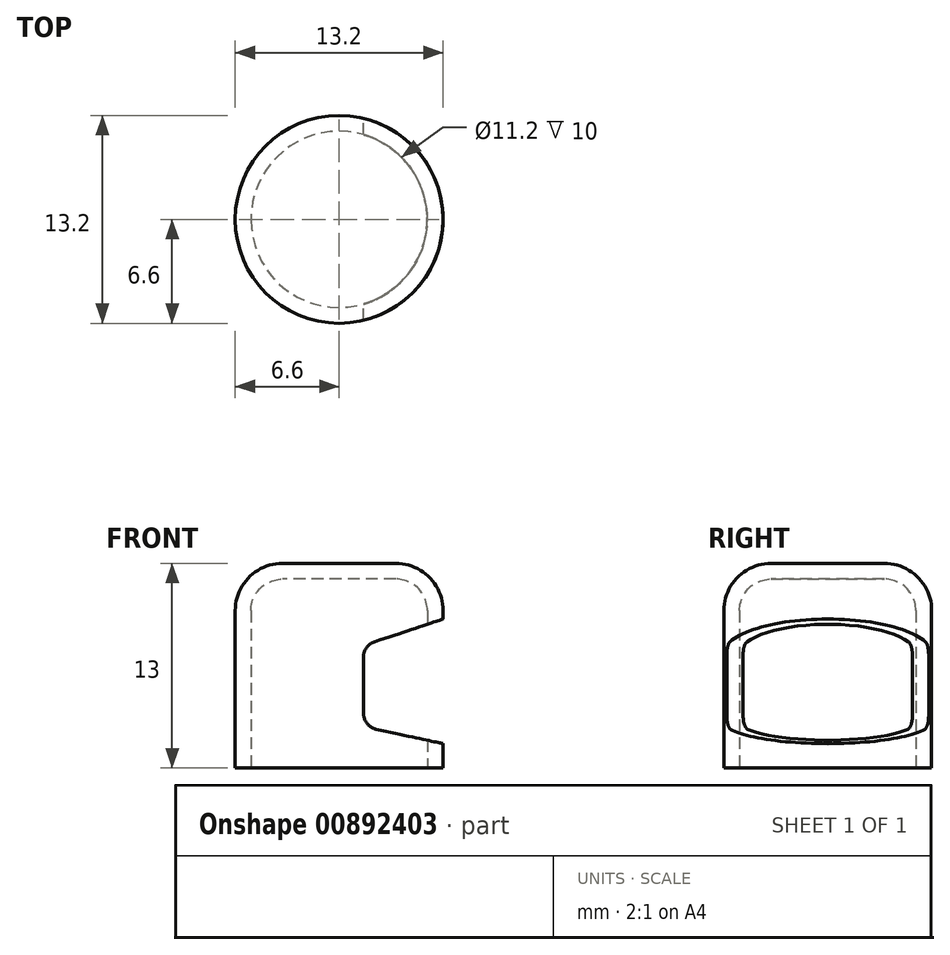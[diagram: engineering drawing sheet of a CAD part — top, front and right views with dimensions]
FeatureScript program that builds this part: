
annotation { "Feature Type Name" : "Feature", "Feature Type Description" : "" }
export const myFeature = defineFeature(function(context is Context, id is Id, definition is map)
    precondition{}
    {
        {
            var Q0;
            Q0=qCreatedBy(makeId("Top.planeOp"),FACE);
            var sketch = newSketch(context, id + "F0", { "sketchPlane" : qUnion([Q0])});
            skCircle(sketch, "E0", {"center": v(0, 0) * mm, "radius": 6.6 * mm});
            skSolve(sketch);
        }
        {
            var Q0;
            Q0=makeQuery(id+"F0.imprint","IMPRINT",FACE,{"disambiguationData":[TD([[makeQuery(id+"F0.imprint","IMPRINT",EDGE,{"derivedFrom":sQuery(id+"F0.wireOp",EDGE,"E0")}),1.0]])]});
            extrude(context, id + "F1", {"entities" : qUnion([Q0]), "depth" : 13 * mm, "offsetDistance" : 25.4 * mm});
        }
        {
            var Q0;
            Q0=makeQuery(id+"F1.opExtrude","CAP_EDGE",EDGE,{"disambiguationData":[OSD([sQuery(id+"F0.wireOp",EDGE,"E0")])],"isStart":false});
            fillet(context, id + "F2", {"entities" : qUnion([Q0]), "radius" : 3 * mm, "tangentPropagation" : true, "allowEdgeOverflow" : false});
        }
        {
            var Q0;
            Q0=makeQuery(id+"F1.opExtrude","CAP_FACE",FACE,{"disambiguationData":[OSD([sQuery(id+"F0.wireOp",EDGE,"E0")])],"isStart":true});
            shell(context, id + "F3", {"entities" : qUnion([Q0]), "thickness" : 1 * mm});
        }
        {
            var Q0;
            Q0=qCreatedBy(makeId("Front.planeOp"),FACE);
            var sketch = newSketch(context, id + "F4", { "sketchPlane" : qUnion([Q0])});
            skLineSegment(sketch, "E1", {"start": v(9, 10.26) * mm, "end": v(2.23, 8.02) * mm});
            skLineSegment(sketch, "E2", {"start": v(1.55, 7.07) * mm, "end": v(1.55, 3.44) * mm});
            skLineSegment(sketch, "E3", {"start": v(2.34, 2.47) * mm, "end": v(9.8, 0.86) * mm});
            skLineSegment(sketch, "E4", {"start": v(9.8, 0.86) * mm, "end": v(9, 10.26) * mm});
            skPoint(sketch, "E5.visualSharp", {"position": v(1.55, 7.8) * mm});
            skArc(sketch, "E5.filletArc", {"start": v(2.23, 8.02) * mm, "mid": v(1.74, 7.66) * mm, "end": v(1.55, 7.07) * mm});
            skPoint(sketch, "E6.visualSharp", {"position": v(1.55, 2.64) * mm});
            skArc(sketch, "E6.filletArc", {"start": v(1.55, 3.44) * mm, "mid": v(1.77, 2.82) * mm, "end": v(2.34, 2.47) * mm});
            skSolve(sketch);
        }
        {
            var Q0;
            Q0=makeQuery(id+"F4.imprint","IMPRINT",FACE,{"disambiguationData":[TD([[makeQuery(id+"F4.imprint","IMPRINT",EDGE,{"derivedFrom":sQuery(id+"F4.wireOp",EDGE,"E1")}),1.0]])]});
            extrude(context, id + "F5", {"entities" : qUnion([Q0]), "operationType" : NewBodyOperationType.REMOVE, "endBound" : BoundingType.SYMMETRIC, "depth" : 30 * mm, "offsetDistance" : 25.4 * mm});
        }
    });
